# Revit family: L-office 32 S Premium
name_source: partatom
category: Осветительные приборы
revit_build: Autodesk Revit 2017 (Build: 20160225_1515(x64)
units: mm (PartAtom-declared; Revit-internal decimal feet)

## family parameters
Всегда вертикально = Да
Заголовок OmniClass = Luminaries for Internal Lighting
Источник света = Да
Номер OmniClass = 23.80.70.11
Общий = Нет
Основа = Потолок
При загрузке вырезать с полостями = Нет
Размер круглого соединителя = Использовать диаметр
Тип детали = Нормальный
Точка расчета площади = Нет

## types (2) — shared parameters
Видимая форма излучения при визуализации = Да
Изготовитель = LEDEL
Излучение по длине прямоугольника = 590 мм
Излучение по ширине прямоугольника = 590 мм
Классификация нагрузок = Освещение
Комментарии к типоразмеру = Офисные
Кривая сил света = Д
Полная установленная мощность = 30 В·А
Световой поток светильника = 2682 лм
Светофильтр = 16777215
Смещение цветовой температуры при затухании лампы = <Нет>
Угол наклона = 90.00°
Файл фотометрической сетки = L-office 32-30-Д-4.0K-02-S-Premium.ies
Цветовая температура = 4000 K

## per-type parameters (varying)
| type | Артикул | Описание | Расстояние от потолка до светильника |
| L-office 32 S Premium 4.0K | 104005 | Светильник L-office 32 S Premium предназначен для установки в образовательных учреждениях (школьные кабинеты, классы, лекционные аудитории и т.п.). | 100 мм |
| L-office 32 S Em Premium 4.0K | 104045 | Светильник c аварийным блоком освещения L-office 32 S Em Premium предназначен для установки в образовательных учреждениях (школьные кабинеты, классы, лекционные аудитории и т.п.). | 150 мм |

## geometry (parser evidence)
native form markers: Sweep x2
no freeform markers — native parametric forms only
